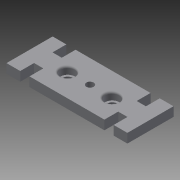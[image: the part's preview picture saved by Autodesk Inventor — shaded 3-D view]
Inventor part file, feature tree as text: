
AUTODESK INVENTOR PART (.ipt)
format: ipt  version: 2015 (Build 190159000, 159)  size: 137,728 bytes
history: native  units: mm
features: extrude x4, sketch x3, fillet x1
ambient origin geometry x8: Origin, YZ Plane, XZ Plane, XY Plane, X Axis, Y Axis, Z Axis, Center Point
bodies: Body1 (feature_tree)
feature tree (8):
  sketch  "Sketch1"  dims[d0=15.0mm d1=15.0mm d2=15.0mm d3=15.0mm d8=15.0mm]
  extrude  "Extrusion2"  Depth=15.0mm
  extrude  "Extrusion3"  Depth=10.0mm TaperAngle=0.0deg
  extrude  "Extrusion6"  Depth=2.0mm
  extrude  "Extrusion7"  Depth=10.0mm TaperAngle=0.0deg
  fillet  "Fillet1"  Radius=48.2mm
  sketch  "Sketch2"  dims[d9=15.0mm d10=10.0mm d11=0.0mm]
  sketch  "Sketch3"  dims[d15=2.5mm d16=2.5mm d17=10.0mm d18=0.0mm d25=48.2mm d26=10.0mm d27=10.0mm d28=2.0mm d29=0.0mm d30=8.0mm d31=10.0mm d32=0.0mm d33=2.0mm]
